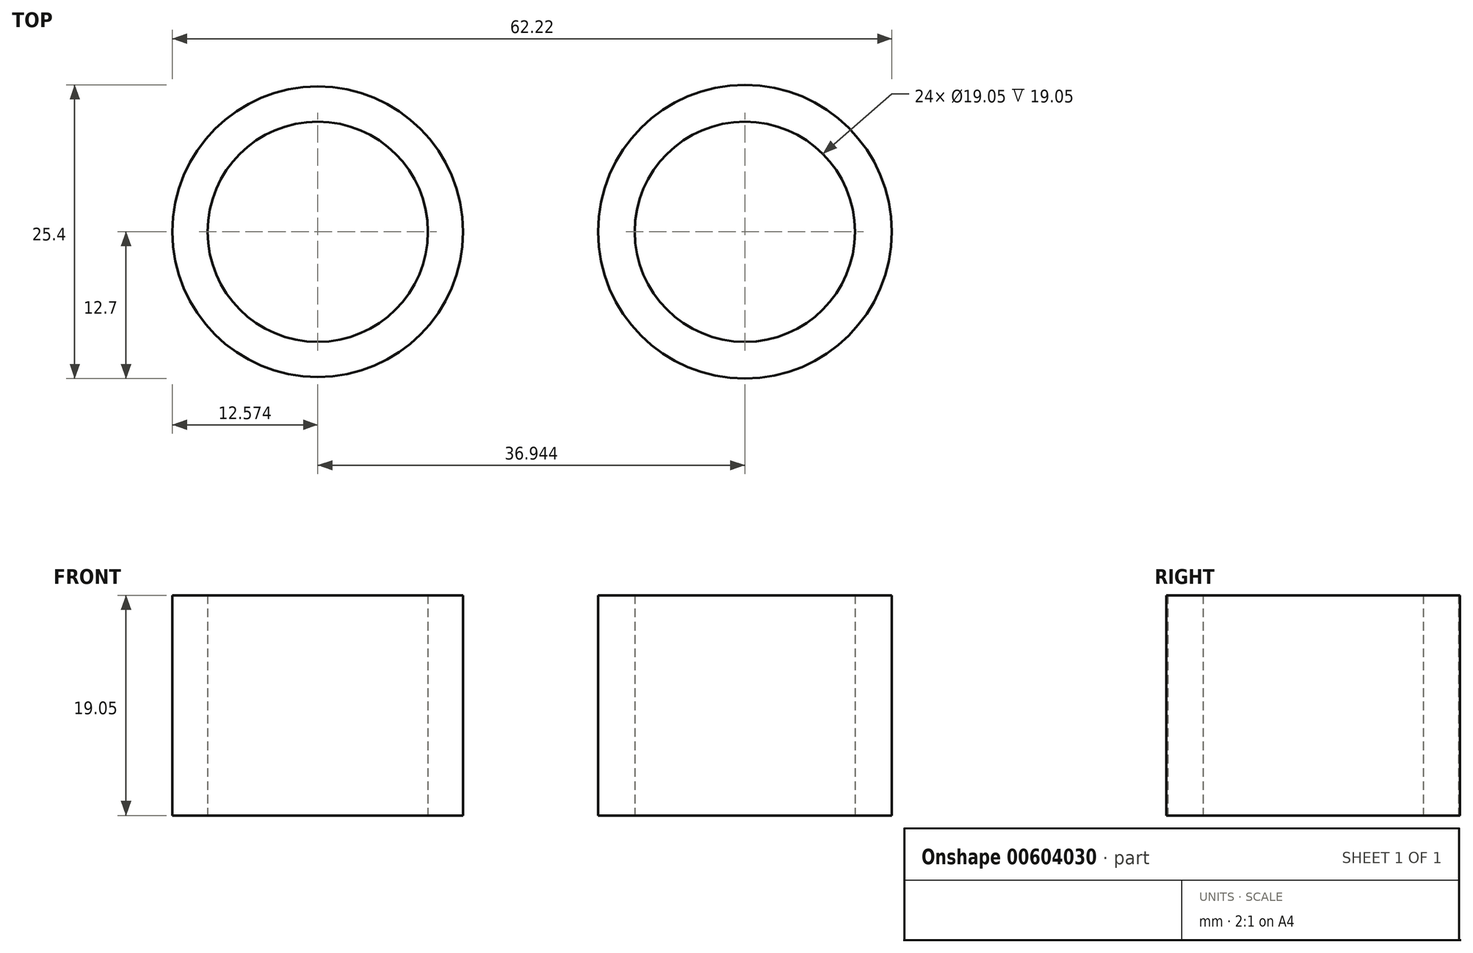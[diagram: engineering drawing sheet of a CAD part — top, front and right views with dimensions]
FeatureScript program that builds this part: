
annotation { "Feature Type Name" : "Feature", "Feature Type Description" : "" }
export const myFeature = defineFeature(function(context is Context, id is Id, definition is map)
    precondition{}
    {
        {
            var Q0;
            Q0=qCreatedBy(makeId("Top.planeOp"),FACE);
            var sketch = newSketch(context, id + "F0", { "sketchPlane" : qUnion([Q0])});
            skCircle(sketch, "E0", {"center": v(25.29, 6.3) * mm, "radius": 12.7 * mm});
            skCircle(sketch, "E1", {"center": v(25.29, 6.3) * mm, "radius": 9.53 * mm});
            skCircle(sketch, "E2", {"center": v(-11.66, 6.3) * mm, "radius": 12.57 * mm});
            skCircle(sketch, "E3", {"center": v(-11.66, 6.3) * mm, "radius": 9.53 * mm});
            skSolve(sketch);
        }
        {
            var Q0;
            Q0 = qSketchRegion(id + "F0", true);
            extrude(context, id + "F1", {"entities" : qUnion([Q0]), "depth" : 19.05 * mm, "offsetDistance" : 25.4 * mm});
        }
    });
